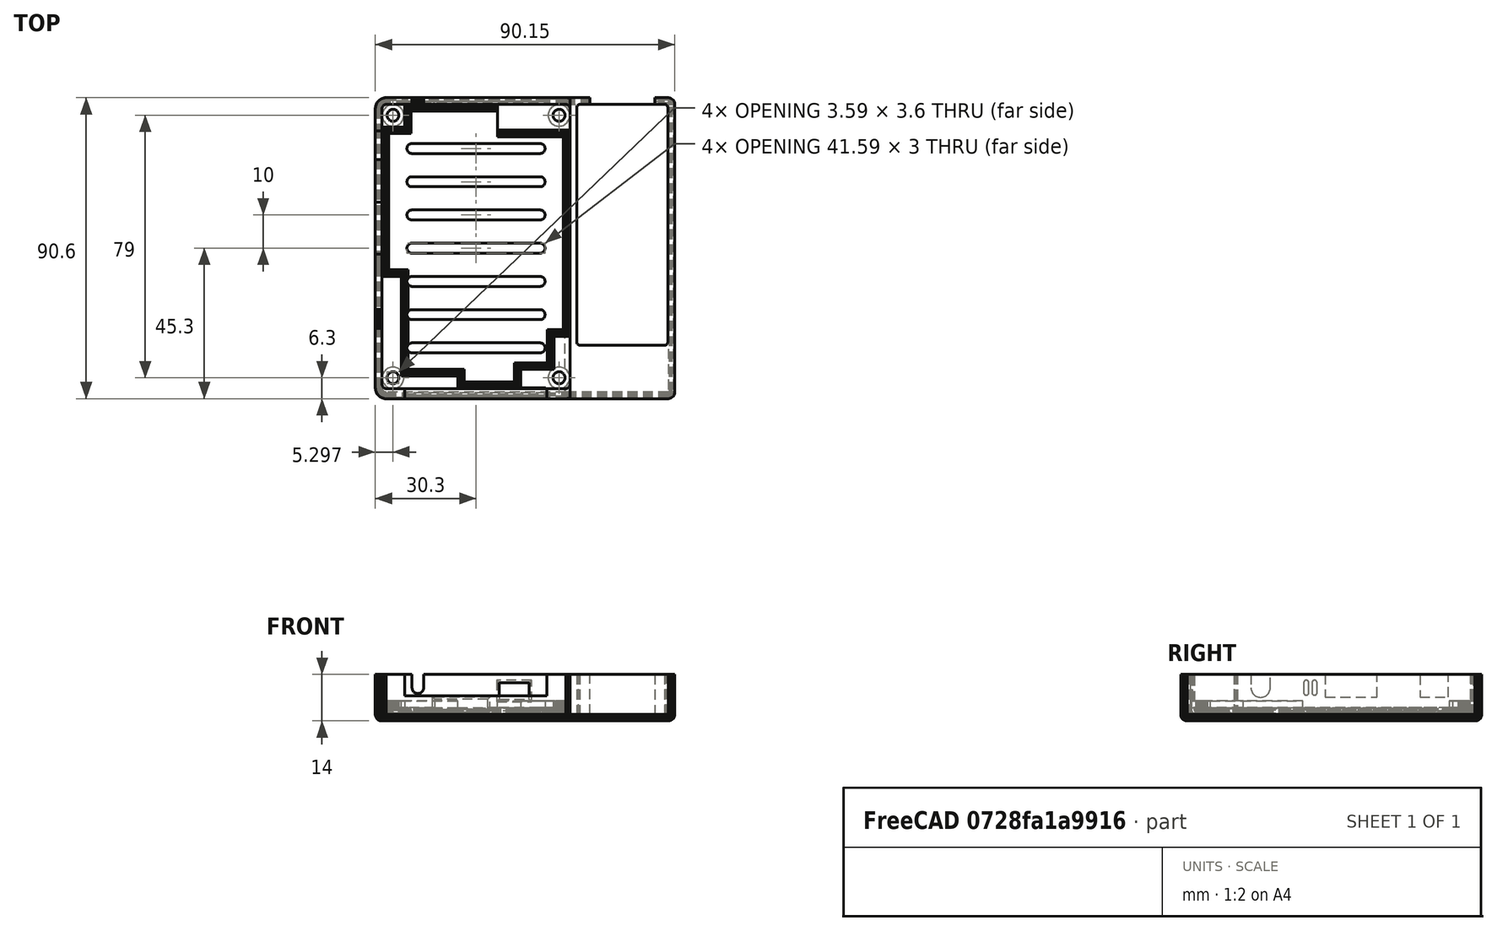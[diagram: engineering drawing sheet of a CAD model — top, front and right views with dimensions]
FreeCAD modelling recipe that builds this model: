
FCSTD DOCUMENT  (FreeCAD 1.0R38806 (Git))
Label: Bottom_STL_Combined
License: All rights reserved
LicenseURL: https://en.wikipedia.org/wiki/All_rights_reserved
objects: Part::Feature×2, PartDesign::FeatureBase×2, PartDesign::Body×2, PartDesign::Boolean×1
note: 10 computed .brp shape members not serialized (recipe doc carries the construction recipe); baked Part::Feature solids carry a one-line shape summary decoded from their .brp

FEATURE [Part::Feature] Bottom_Extension_Model001_solid  label="Bottom_Extension_Model"
  shape: bbox 33 x 90.6 x 14 mm, 468 faces (baked)
FEATURE [Part::Feature] Orange_PI_PC_Case_Bottom001_solid  label="Orange_PI_PC_Case_Bottom"
  Placement = pos=(0,0,6) rot=(0,0,1;0rad)
  shape: bbox 60.6 x 90.6 x 14 mm, 7522 faces (baked)
FEATURE [PartDesign::FeatureBase] BaseFeature001  label="Bottom_Extension_Base"
  BaseFeature = -> Bottom_Extension_Model001_solid
  Suppressed = false
FEATURE [PartDesign::Body] Body001  label="Bottom_Extension"
  AllowCompound = false
  BaseFeature = -> Bottom_Extension_Model001_solid
  Group = -> [BaseFeature001]
  Origin = -> Origin001
  Tip = -> BaseFeature001
FEATURE [PartDesign::FeatureBase] BaseFeature  label="Bottom_Case_Base"
  BaseFeature = -> Orange_PI_PC_Case_Bottom001_solid
  Placement = pos=(0,0,6) rot=(0,0,1;0rad)
  Suppressed = false
FEATURE [PartDesign::Boolean] Boolean
  Group = -> [BaseFeature,Bottom_Extension_Model001_solid,Body001]
  Refine = true
  Suppressed = false
  Type = 0
  UsePlacement = true
FEATURE [PartDesign::Body] Body  label="Bottom_Case"
  AllowCompound = false
  Group = -> [Boolean]
  Origin = -> Origin
  Tip = -> Boolean
